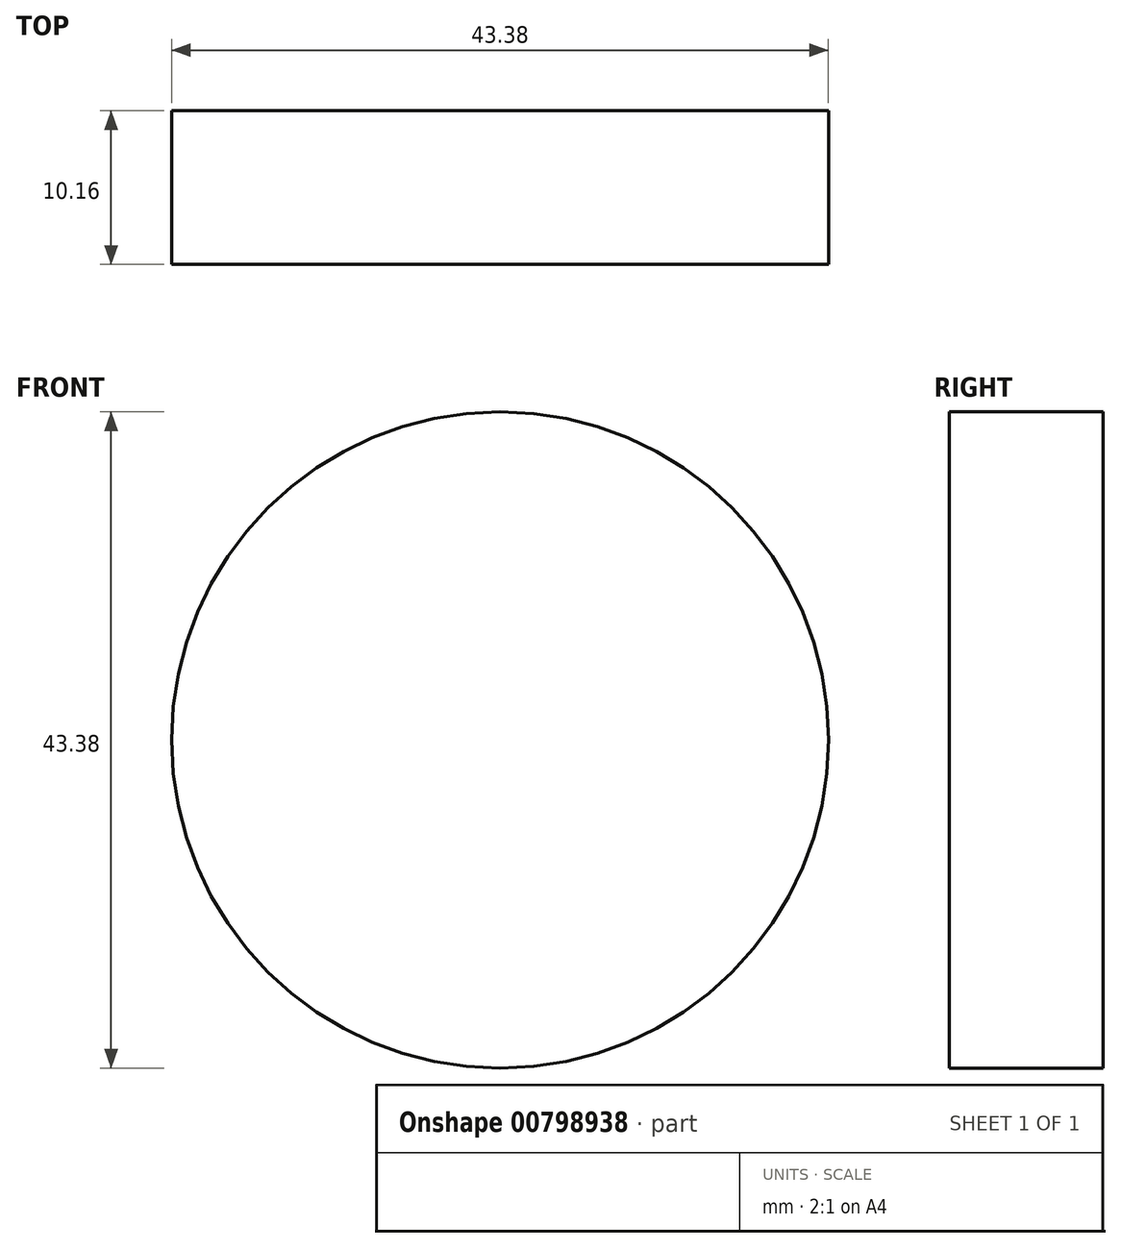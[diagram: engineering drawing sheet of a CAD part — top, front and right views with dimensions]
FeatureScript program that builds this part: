
annotation { "Feature Type Name" : "Feature", "Feature Type Description" : "" }
export const myFeature = defineFeature(function(context is Context, id is Id, definition is map)
    precondition{}
    {
        {
            var Q0;
            Q0=qCreatedBy(makeId("Front.planeOp"),FACE);
            var sketch = newSketch(context, id + "F0", { "sketchPlane" : qUnion([Q0])});
            skCircle(sketch, "E0", {"center": v(0, 0) * mm, "radius": 21.7 * mm});
            skSolve(sketch);
        }
        {
            var Q0;
            Q0=makeQuery(id+"F0.imprint","IMPRINT",FACE,{"disambiguationData":[TD([[makeQuery(id+"F0.imprint","IMPRINT",EDGE,{"derivedFrom":sQuery(id+"F0.wireOp",EDGE,"E0")}),1.0]])]});
            extrude(context, id + "F1", {"entities" : qUnion([Q0]), "depth" : 10.16 * mm, "offsetDistance" : 25.4 * mm});
        }
    });
